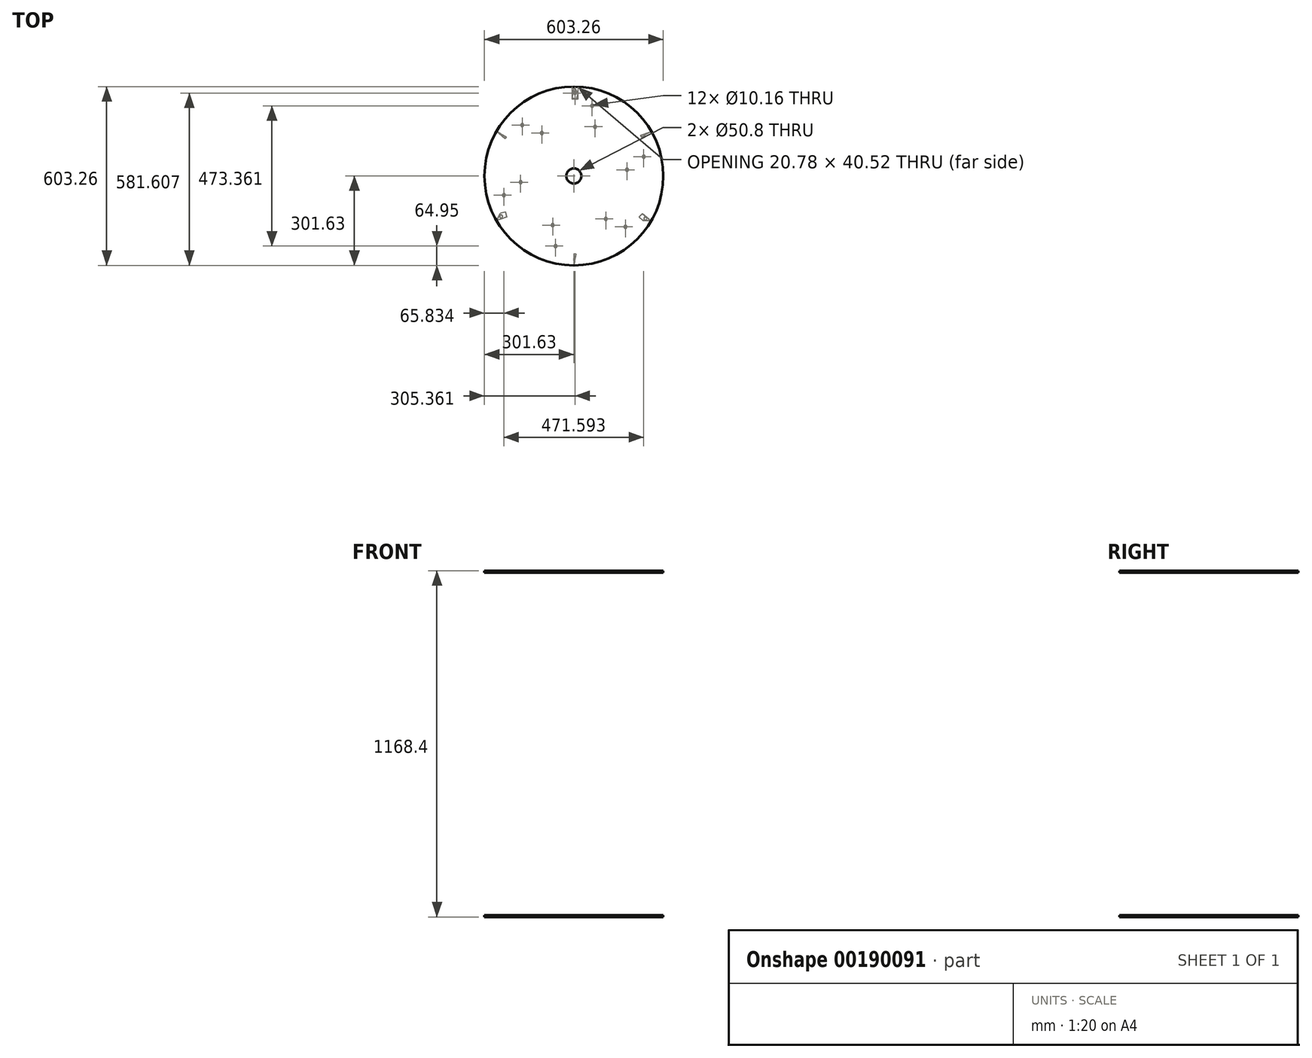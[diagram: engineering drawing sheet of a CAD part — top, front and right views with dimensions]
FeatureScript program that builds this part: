
annotation { "Feature Type Name" : "Feature", "Feature Type Description" : "" }
export const myFeature = defineFeature(function(context is Context, id is Id, definition is map)
    precondition{}
    {
        {
            var Q0;
            Q0=qCreatedBy(makeId("Top.planeOp"),FACE);
            var sketch = newSketch(context, id + "F0", { "sketchPlane" : qUnion([Q0])});
            skCircle(sketch, "E0", {"center": v(0, 0) * mm, "radius": 301.63 * mm});
            skCircle(sketch, "E1", {"center": v(0, 0) * mm, "radius": 25.4 * mm});
            skSolve(sketch);
        }
        {
            var Q0;
            Q0 = qSketchRegion(id + "F0", true);
            extrude(context, id + "F1", {"entities" : qUnion([Q0]), "depth" : 6.35 * mm});
        }
        {
            var Q0;
            Q0=makeQuery(id+"F1.opExtrude","CAP_FACE",FACE,{"disambiguationData":[OSD([sQuery(id+"F0.wireOp",EDGE,"E0"),sQuery(id+"F0.wireOp",EDGE,"E1")])],"isStart":false});
            var sketch = newSketch(context, id + "F2", { "sketchPlane" : qUnion([Q0])});
            skPoint(sketch, "E2.center", {"position": v(0, 0) * mm});
            skArc(sketch, "E3", {"start": v(87.34, 148.3) * mm, "mid": v(73.26, 252.31) * mm, "end": v(-19.74, 300.98) * mm});
            skArc(sketch, "E4", {"start": v(186.63, 0) * mm, "mid": v(255, 58.04) * mm, "end": v(260.45, 147.56) * mm});
            skArc(sketch, "E5", {"start": v(83.88, -151.75) * mm, "mid": v(170.95, -192) * mm, "end": v(258.02, -151.75) * mm});
            skArc(sketch, "E6", {"start": v(-87.35, -148.3) * mm, "mid": v(-78.67, -243.83) * mm, "end": v(-0.27, -299.1) * mm});
            skArc(sketch, "E7", {"start": v(-169.53, 0) * mm, "mid": v(-253.86, -64.43) * mm, "end": v(-248.85, -170.44) * mm});
            skArc(sketch, "E8", {"start": v(-88.68, 150.81) * mm, "mid": v(-172.82, 187.75) * mm, "end": v(-256.96, 150.81) * mm});
            skArc(sketch, "E9", {"start": v(-86.04, 153.57) * mm, "mid": v(-172.82, 191.56) * mm, "end": v(-259.6, 153.57) * mm});
            skLineSegment(sketch, "E10", {"start": v(-86.04, 153.57) * mm, "end": v(-88.68, 150.81) * mm});
            skLineSegment(sketch, "E11", {"start": v(-259.6, 153.57) * mm, "end": v(-256.96, 150.81) * mm});
            skLineSegment(sketch, "E12", {"start": v(0, 0) * mm, "end": v(-172.82, 73.45) * mm});
            skLineSegment(sketch, "E13", {"start": v(0, 0) * mm, "end": v(-20.32, 186.68) * mm});
            skLineSegment(sketch, "E14", {"start": v(0, 0) * mm, "end": v(152.79, 109.17) * mm});
            skLineSegment(sketch, "E15", {"start": v(0, 0) * mm, "end": v(170.95, -77.7) * mm});
            skLineSegment(sketch, "E16", {"start": v(0, 0) * mm, "end": v(20.32, -186.68) * mm});
            skLineSegment(sketch, "E17", {"start": v(0, 0) * mm, "end": v(-150.23, -112.66) * mm});
            skArc(sketch, "E18.1.0", {"start": v(-176.01, 2.28) * mm, "mid": v(-252.3, -53.88) * mm, "end": v(-262.8, -148.04) * mm});
            skArc(sketch, "E18.1.1", {"start": v(-174.95, -1.39) * mm, "mid": v(-249, -55.79) * mm, "end": v(-259.09, -147.13) * mm});
            skLineSegment(sketch, "E18.1.2", {"start": v(-176.01, 2.28) * mm, "end": v(-174.95, -1.39) * mm});
            skLineSegment(sketch, "E18.1.3", {"start": v(-262.8, -148.04) * mm, "end": v(-259.09, -147.13) * mm});
            skArc(sketch, "E18.2.0", {"start": v(-89.98, -151.3) * mm, "mid": v(-79.49, -245.45) * mm, "end": v(-3.2, -301.6) * mm});
            skArc(sketch, "E18.2.1", {"start": v(-86.27, -152.2) * mm, "mid": v(-76.2, -243.54) * mm, "end": v(-2.13, -297.94) * mm});
            skLineSegment(sketch, "E18.2.2", {"start": v(-89.98, -151.3) * mm, "end": v(-86.27, -152.2) * mm});
            skLineSegment(sketch, "E18.2.3", {"start": v(-3.2, -301.6) * mm, "end": v(-2.13, -297.94) * mm});
            skArc(sketch, "E18.3.0", {"start": v(86.04, -153.57) * mm, "mid": v(172.82, -191.56) * mm, "end": v(259.6, -153.57) * mm});
            skArc(sketch, "E18.3.1", {"start": v(88.68, -150.81) * mm, "mid": v(172.82, -187.75) * mm, "end": v(256.96, -150.81) * mm});
            skLineSegment(sketch, "E18.3.2", {"start": v(86.04, -153.57) * mm, "end": v(88.68, -150.81) * mm});
            skLineSegment(sketch, "E18.3.3", {"start": v(259.6, -153.57) * mm, "end": v(256.96, -150.81) * mm});
            skArc(sketch, "E18.4.0", {"start": v(176.01, -2.28) * mm, "mid": v(252.3, 53.88) * mm, "end": v(262.8, 148.04) * mm});
            skArc(sketch, "E18.4.1", {"start": v(174.95, 1.39) * mm, "mid": v(249, 55.79) * mm, "end": v(259.09, 147.13) * mm});
            skLineSegment(sketch, "E18.4.2", {"start": v(176.01, -2.28) * mm, "end": v(174.95, 1.39) * mm});
            skLineSegment(sketch, "E18.4.3", {"start": v(262.8, 148.04) * mm, "end": v(259.09, 147.13) * mm});
            skArc(sketch, "E18.5.0", {"start": v(89.98, 151.3) * mm, "mid": v(79.49, 245.45) * mm, "end": v(3.2, 301.6) * mm});
            skArc(sketch, "E18.5.1", {"start": v(86.27, 152.2) * mm, "mid": v(76.2, 243.54) * mm, "end": v(2.13, 297.94) * mm});
            skLineSegment(sketch, "E18.5.2", {"start": v(89.98, 151.3) * mm, "end": v(86.27, 152.2) * mm});
            skLineSegment(sketch, "E18.5.3", {"start": v(3.2, 301.6) * mm, "end": v(2.13, 297.94) * mm});
            skSolve(sketch);
        }
        {
            var Q0;
            Q0 = qSketchRegion(id + "F2", true);
            var Q1;
            Q1=sQuery(id+"F2.wireOp",EDGE,"E8");
            var Q2;
            Q2=sQuery(id+"F2.wireOp",EDGE,"E3");
            var Q3;
            Q3=sQuery(id+"F2.wireOp",EDGE,"E4");
            var Q4;
            Q4=sQuery(id+"F2.wireOp",EDGE,"E5");
            var Q5;
            Q5=sQuery(id+"F2.wireOp",EDGE,"E6");
            var Q6;
            Q6=sQuery(id+"F2.wireOp",EDGE,"E7");
            extrude(context, id + "F3", {"entities" : qUnion([Q0]), "bodyType" : ToolBodyType.SURFACE, "surfaceEntities" : qUnion([Q1, Q2, Q3, Q4, Q5, Q6]), "depth" : 1155.7 * mm});
        }
        {
            var Q0;
            Q0=makeQuery(id+"F1.opExtrude","CAP_FACE",FACE,{"disambiguationData":[OSD([sQuery(id+"F0.wireOp",EDGE,"E0"),sQuery(id+"F0.wireOp",EDGE,"E1")])],"isStart":false});
            cPlane(context, id + "F4", {"entities" : qUnion([Q0]), "cplaneType" : CPlaneType.OFFSET, "offset" : 1155.7 * mm, "width" : 152.4 * mm, "height" : 152.4 * mm});
        }
        {
            var Q0;
            Q0=qCreatedBy(id+"F4.planeOp",FACE);
            var sketch = newSketch(context, id + "F5", { "sketchPlane" : qUnion([Q0])});
            skCircle(sketch, "E19", {"center": v(0, 0) * mm, "radius": 301.63 * mm});
            skCircle(sketch, "E20", {"center": v(0, 0) * mm, "radius": 25.4 * mm});
            skSolve(sketch);
        }
        {
            var Q0;
            Q0=makeQuery(id+"F1.opExtrude","CAP_FACE",FACE,{"disambiguationData":[OSD([sQuery(id+"F0.wireOp",EDGE,"E0"),sQuery(id+"F0.wireOp",EDGE,"E1")])],"isStart":false});
            var sketch = newSketch(context, id + "F6", { "sketchPlane" : qUnion([Q0])});
            skLineSegment(sketch, "E21", {"start": v(261.58, 150.18) * mm, "end": v(167.94, 150.18) * mm});
            skLineSegment(sketch, "E22", {"start": v(0, 0) * mm, "end": v(0, -301.63) * mm});
            skLineSegment(sketch, "E23.1.0", {"start": v(0, 0) * mm, "end": v(261.21, 150.81) * mm});
            skLineSegment(sketch, "E23.2.0", {"start": v(0, 0) * mm, "end": v(-261.21, 150.81) * mm});
            skPoint(sketch, "E23.center", {"position": v(0, 0) * mm});
            skLineSegment(sketch, "E24", {"start": v(261.58, 150.18) * mm, "end": v(0, -301.63) * mm});
            skLineSegment(sketch, "E25", {"start": v(0, -301.63) * mm, "end": v(-261.21, 150.81) * mm});
            skLineSegment(sketch, "E26", {"start": v(-261.21, 150.81) * mm, "end": v(261.58, 150.18) * mm});
            skLineSegment(sketch, "E27.1.0", {"start": v(-261.26, -151.02) * mm, "end": v(0.32, 300.79) * mm});
            skLineSegment(sketch, "E27.1.1", {"start": v(0.32, 300.79) * mm, "end": v(261.53, -151.65) * mm});
            skLineSegment(sketch, "E27.1.2", {"start": v(261.53, -151.65) * mm, "end": v(-261.26, -151.02) * mm});
            skPoint(sketch, "E27.center", {"position": v(0.16, -0.42) * mm});
            skArc(sketch, "E28", {"start": v(-173.98, -0.28) * mm, "mid": v(-252.48, -55.47) * mm, "end": v(-261.26, -151.02) * mm});
            skLineSegment(sketch, "E29", {"start": v(-173.98, -0.28) * mm, "end": v(-153.56, -112.74) * mm});
            skLineSegment(sketch, "E30", {"start": v(-153.56, -112.74) * mm, "end": v(-261.26, -151.02) * mm});
            skLineSegment(sketch, "E31", {"start": v(-86.63, 150.6) * mm, "end": v(-174.01, 76.92) * mm});
            skLineSegment(sketch, "E32", {"start": v(-174.01, 76.92) * mm, "end": v(-261.21, 150.81) * mm});
            skLineSegment(sketch, "E33", {"start": v(0.32, 300.79) * mm, "end": v(-21, 188.5) * mm});
            skLineSegment(sketch, "E34", {"start": v(-21, 188.5) * mm, "end": v(86.9, 150.81) * mm});
            skLineSegment(sketch, "E35", {"start": v(174.63, 0) * mm, "end": v(153.71, 112.37) * mm});
            skLineSegment(sketch, "E36", {"start": v(153.71, 112.37) * mm, "end": v(261.58, 150.18) * mm});
            skLineSegment(sketch, "E37", {"start": v(86.95, -151.44) * mm, "end": v(174.33, -77.76) * mm});
            skLineSegment(sketch, "E38", {"start": v(174.33, -77.76) * mm, "end": v(261.53, -151.65) * mm});
            skLineSegment(sketch, "E39", {"start": v(0, -301.63) * mm, "end": v(21.86, -189.43) * mm});
            skLineSegment(sketch, "E40", {"start": v(21.86, -189.43) * mm, "end": v(-86.83, -151.23) * mm});
            skLineSegment(sketch, "E41", {"start": v(165.28, 37) * mm, "end": v(175.1, 0.19) * mm});
            skLineSegment(sketch, "E42", {"start": v(165.28, 37) * mm, "end": v(183.69, 41.9) * mm});
            skLineSegment(sketch, "E43", {"start": v(183.69, 41.9) * mm, "end": v(193.5, 5.1) * mm});
            skLineSegment(sketch, "E44", {"start": v(175.1, 0.19) * mm, "end": v(193.5, 5.1) * mm});
            skCircle(sketch, "E45", {"center": v(179.4, 21.05) * mm, "radius": 5.08 * mm});
            skLineSegment(sketch, "E46.1.0", {"start": v(87.39, 151.73) * mm, "end": v(92.34, 170.13) * mm});
            skLineSegment(sketch, "E46.1.1", {"start": v(50.6, 161.64) * mm, "end": v(87.39, 151.73) * mm});
            skLineSegment(sketch, "E46.1.2", {"start": v(55.55, 180.03) * mm, "end": v(92.34, 170.13) * mm});
            skCircle(sketch, "E46.1.3", {"center": v(71.47, 165.88) * mm, "radius": 5.08 * mm});
            skLineSegment(sketch, "E46.1.4", {"start": v(50.6, 161.64) * mm, "end": v(55.55, 180.03) * mm});
            skLineSegment(sketch, "E46.2.0", {"start": v(-87.71, 151.55) * mm, "end": v(-101.17, 165.03) * mm});
            skLineSegment(sketch, "E46.2.1", {"start": v(-114.68, 124.64) * mm, "end": v(-87.71, 151.55) * mm});
            skLineSegment(sketch, "E46.2.2", {"start": v(-128.14, 138.13) * mm, "end": v(-101.17, 165.03) * mm});
            skCircle(sketch, "E46.2.3", {"center": v(-107.93, 144.84) * mm, "radius": 5.08 * mm});
            skLineSegment(sketch, "E46.2.4", {"start": v(-114.68, 124.64) * mm, "end": v(-128.14, 138.13) * mm});
            skLineSegment(sketch, "E47.1.3.0", {"start": v(-175.1, -0.19) * mm, "end": v(-193.5, -5.1) * mm});
            skLineSegment(sketch, "E47.3.3.0", {"start": v(-165.28, -37) * mm, "end": v(-175.1, -0.19) * mm});
            skLineSegment(sketch, "E47.6.3.0", {"start": v(-183.69, -41.9) * mm, "end": v(-193.5, -5.1) * mm});
            skCircle(sketch, "E47.9.3.0", {"center": v(-179.4, -21.05) * mm, "radius": 5.08 * mm});
            skLineSegment(sketch, "E47.11.3.0", {"start": v(-165.28, -37) * mm, "end": v(-183.69, -41.9) * mm});
            skLineSegment(sketch, "E47.1.4.0", {"start": v(-87.39, -151.73) * mm, "end": v(-92.34, -170.13) * mm});
            skLineSegment(sketch, "E47.3.4.0", {"start": v(-50.6, -161.64) * mm, "end": v(-87.39, -151.73) * mm});
            skLineSegment(sketch, "E47.6.4.0", {"start": v(-55.55, -180.03) * mm, "end": v(-92.34, -170.13) * mm});
            skCircle(sketch, "E47.9.4.0", {"center": v(-71.47, -165.88) * mm, "radius": 5.08 * mm});
            skLineSegment(sketch, "E47.11.4.0", {"start": v(-50.6, -161.64) * mm, "end": v(-55.55, -180.03) * mm});
            skLineSegment(sketch, "E47.1.5.0", {"start": v(87.71, -151.55) * mm, "end": v(101.17, -165.03) * mm});
            skLineSegment(sketch, "E47.3.5.0", {"start": v(114.68, -124.64) * mm, "end": v(87.71, -151.55) * mm});
            skLineSegment(sketch, "E47.6.5.0", {"start": v(128.14, -138.13) * mm, "end": v(101.17, -165.03) * mm});
            skCircle(sketch, "E47.9.5.0", {"center": v(107.93, -144.84) * mm, "radius": 5.08 * mm});
            skLineSegment(sketch, "E47.11.5.0", {"start": v(114.68, -124.64) * mm, "end": v(128.14, -138.13) * mm});
            skLineSegment(sketch, "E48.MirrorCS", {"start": v(-9.55, -259.72) * mm, "end": v(-19.36, -296.53) * mm});
            skLineSegment(sketch, "E49.MirrorCS", {"start": v(-0.96, -301.44) * mm, "end": v(-19.36, -296.53) * mm});
            skCircle(sketch, "E50.MirrorC", {"center": v(-3.99, -280.82) * mm, "radius": 5.08 * mm});
            skLineSegment(sketch, "E51.MirrorCS", {"start": v(8.86, -264.62) * mm, "end": v(-9.55, -259.72) * mm});
            skLineSegment(sketch, "E52.MirrorCS", {"start": v(8.86, -264.62) * mm, "end": v(-0.96, -301.44) * mm});
            skLineSegment(sketch, "E53.1.0", {"start": v(260.57, -151.55) * mm, "end": v(247.12, -165.03) * mm});
            skLineSegment(sketch, "E53.1.1", {"start": v(220.15, -138.13) * mm, "end": v(247.12, -165.03) * mm});
            skLineSegment(sketch, "E53.1.2", {"start": v(233.6, -124.64) * mm, "end": v(260.57, -151.55) * mm});
            skLineSegment(sketch, "E53.1.3", {"start": v(233.6, -124.64) * mm, "end": v(220.15, -138.13) * mm});
            skCircle(sketch, "E53.1.4", {"center": v(241.2, -143.86) * mm, "radius": 5.08 * mm});
            skLineSegment(sketch, "E53.2.0", {"start": v(261.53, 149.9) * mm, "end": v(266.48, 131.5) * mm});
            skLineSegment(sketch, "E53.2.1", {"start": v(229.7, 121.6) * mm, "end": v(266.48, 131.5) * mm});
            skLineSegment(sketch, "E53.2.2", {"start": v(224.74, 139.99) * mm, "end": v(261.53, 149.9) * mm});
            skLineSegment(sketch, "E53.2.3", {"start": v(224.74, 139.99) * mm, "end": v(229.7, 121.6) * mm});
            skCircle(sketch, "E53.2.4", {"center": v(245.19, 136.96) * mm, "radius": 5.08 * mm});
            skLineSegment(sketch, "E54.2.3.0", {"start": v(0.96, 301.44) * mm, "end": v(19.36, 296.53) * mm});
            skLineSegment(sketch, "E54.3.3.0", {"start": v(9.55, 259.72) * mm, "end": v(19.36, 296.53) * mm});
            skLineSegment(sketch, "E54.6.3.0", {"start": v(-8.86, 264.62) * mm, "end": v(0.96, 301.44) * mm});
            skLineSegment(sketch, "E54.9.3.0", {"start": v(-8.86, 264.62) * mm, "end": v(9.55, 259.72) * mm});
            skCircle(sketch, "E54.12.3.0", {"center": v(3.99, 280.82) * mm, "radius": 5.08 * mm});
            skLineSegment(sketch, "E54.2.4.0", {"start": v(-260.57, 151.55) * mm, "end": v(-247.12, 165.03) * mm});
            skLineSegment(sketch, "E54.3.4.0", {"start": v(-220.15, 138.13) * mm, "end": v(-247.12, 165.03) * mm});
            skLineSegment(sketch, "E54.6.4.0", {"start": v(-233.6, 124.64) * mm, "end": v(-260.57, 151.55) * mm});
            skLineSegment(sketch, "E54.9.4.0", {"start": v(-233.6, 124.64) * mm, "end": v(-220.15, 138.13) * mm});
            skCircle(sketch, "E54.12.4.0", {"center": v(-241.2, 143.86) * mm, "radius": 5.08 * mm});
            skLineSegment(sketch, "E54.2.5.0", {"start": v(-261.53, -149.9) * mm, "end": v(-266.48, -131.5) * mm});
            skLineSegment(sketch, "E54.3.5.0", {"start": v(-229.7, -121.6) * mm, "end": v(-266.48, -131.5) * mm});
            skLineSegment(sketch, "E54.6.5.0", {"start": v(-224.74, -139.99) * mm, "end": v(-261.53, -149.9) * mm});
            skLineSegment(sketch, "E54.9.5.0", {"start": v(-224.74, -139.99) * mm, "end": v(-229.7, -121.6) * mm});
            skCircle(sketch, "E54.12.5.0", {"center": v(-245.19, -136.96) * mm, "radius": 5.08 * mm});
            skCircle(sketch, "E55", {"center": v(-61.65, -236.68) * mm, "radius": 5.08 * mm});
            skLineSegment(sketch, "E56", {"start": v(-78.31, -246.3) * mm, "end": v(-83.08, -238.05) * mm});
            skLineSegment(sketch, "E57", {"start": v(-83.08, -238.05) * mm, "end": v(-50.08, -219) * mm});
            skLineSegment(sketch, "E58", {"start": v(-50.08, -219) * mm, "end": v(-40.56, -235.5) * mm});
            skLineSegment(sketch, "E59", {"start": v(-40.56, -235.5) * mm, "end": v(-73.55, -254.55) * mm});
            skLineSegment(sketch, "E60", {"start": v(-73.55, -254.55) * mm, "end": v(-83.08, -238.05) * mm});
            skLineSegment(sketch, "E61.1.0", {"start": v(164.62, -152.87) * mm, "end": v(183.67, -152.87) * mm});
            skLineSegment(sketch, "E61.1.1", {"start": v(164.62, -190.97) * mm, "end": v(164.62, -152.87) * mm});
            skCircle(sketch, "E61.1.2", {"center": v(174.15, -171.73) * mm, "radius": 5.08 * mm});
            skLineSegment(sketch, "E61.1.3", {"start": v(183.67, -152.87) * mm, "end": v(183.67, -190.97) * mm});
            skLineSegment(sketch, "E61.1.4", {"start": v(174.15, -190.97) * mm, "end": v(164.62, -190.97) * mm});
            skLineSegment(sketch, "E61.1.5", {"start": v(183.67, -190.97) * mm, "end": v(164.62, -190.97) * mm});
            skLineSegment(sketch, "E61.2.0", {"start": v(214.7, 66.13) * mm, "end": v(224.23, 82.63) * mm});
            skLineSegment(sketch, "E61.2.1", {"start": v(247.7, 47.08) * mm, "end": v(214.7, 66.13) * mm});
            skCircle(sketch, "E61.2.2", {"center": v(235.8, 64.95) * mm, "radius": 5.08 * mm});
            skLineSegment(sketch, "E61.2.3", {"start": v(224.23, 82.63) * mm, "end": v(257.22, 63.58) * mm});
            skLineSegment(sketch, "E61.2.4", {"start": v(252.46, 55.33) * mm, "end": v(247.7, 47.08) * mm});
            skLineSegment(sketch, "E61.2.5", {"start": v(257.22, 63.58) * mm, "end": v(247.7, 47.08) * mm});
            skLineSegment(sketch, "E61.3.0", {"start": v(50.08, 219) * mm, "end": v(40.56, 235.5) * mm});
            skLineSegment(sketch, "E61.3.1", {"start": v(83.08, 238.05) * mm, "end": v(50.08, 219) * mm});
            skCircle(sketch, "E61.3.2", {"center": v(61.65, 236.68) * mm, "radius": 5.08 * mm});
            skLineSegment(sketch, "E61.3.3", {"start": v(40.56, 235.5) * mm, "end": v(73.55, 254.55) * mm});
            skLineSegment(sketch, "E61.3.4", {"start": v(78.31, 246.3) * mm, "end": v(83.08, 238.05) * mm});
            skLineSegment(sketch, "E61.3.5", {"start": v(73.55, 254.55) * mm, "end": v(83.08, 238.05) * mm});
            skLineSegment(sketch, "E61.4.0", {"start": v(-164.62, 152.87) * mm, "end": v(-183.67, 152.87) * mm});
            skLineSegment(sketch, "E61.4.1", {"start": v(-164.62, 190.97) * mm, "end": v(-164.62, 152.87) * mm});
            skCircle(sketch, "E61.4.2", {"center": v(-174.15, 171.73) * mm, "radius": 5.08 * mm});
            skLineSegment(sketch, "E61.4.3", {"start": v(-183.67, 152.87) * mm, "end": v(-183.67, 190.97) * mm});
            skLineSegment(sketch, "E61.4.4", {"start": v(-174.15, 190.97) * mm, "end": v(-164.62, 190.97) * mm});
            skLineSegment(sketch, "E61.4.5", {"start": v(-183.67, 190.97) * mm, "end": v(-164.62, 190.97) * mm});
            skLineSegment(sketch, "E61.5.0", {"start": v(-214.7, -66.13) * mm, "end": v(-224.23, -82.63) * mm});
            skLineSegment(sketch, "E61.5.1", {"start": v(-247.7, -47.08) * mm, "end": v(-214.7, -66.13) * mm});
            skCircle(sketch, "E61.5.2", {"center": v(-235.8, -64.95) * mm, "radius": 5.08 * mm});
            skLineSegment(sketch, "E61.5.3", {"start": v(-224.23, -82.63) * mm, "end": v(-257.22, -63.58) * mm});
            skLineSegment(sketch, "E61.5.4", {"start": v(-252.46, -55.33) * mm, "end": v(-247.7, -47.08) * mm});
            skLineSegment(sketch, "E61.5.5", {"start": v(-257.22, -63.58) * mm, "end": v(-247.7, -47.08) * mm});
            skSolve(sketch);
        }
        {
            var Q0;
            Q0 = qSketchRegion(id + "F5", true);
            extrude(context, id + "F7", {"entities" : qUnion([Q0]), "depth" : 6.35 * mm});
        }
        {
            var Q0;
            Q0=makeQuery(id+"F6.imprint","IMPRINT",FACE,{"disambiguationData":[TD([[makeQuery(id+"F6.imprint","IMPRINT",EDGE,{"derivedFrom":sQuery(id+"F6.wireOp",EDGE,"E54.12.4.0")}),-1.0]])]});
            var Q1;
            Q1=makeQuery(id+"F6.imprint","IMPRINT",FACE,{"disambiguationData":[TD([[makeQuery(id+"F6.imprint","IMPRINT",EDGE,{"derivedFrom":sQuery(id+"F6.wireOp",EDGE,"E61.4.2")}),1.0]])]});
            var Q2;
            Q2=makeQuery(id+"F6.imprint","IMPRINT",FACE,{"disambiguationData":[TD([[makeQuery(id+"F6.imprint","IMPRINT",EDGE,{"derivedFrom":sQuery(id+"F6.wireOp",EDGE,"E46.2.3")}),1.0]])]});
            var Q3;
            Q3=makeQuery(id+"F6.imprint","IMPRINT",FACE,{"disambiguationData":[TD([[makeQuery(id+"F6.imprint","IMPRINT",EDGE,{"derivedFrom":sQuery(id+"F6.wireOp",EDGE,"E54.12.5.0")}),-1.0]])]});
            var Q4;
            Q4=makeQuery(id+"F6.imprint","IMPRINT",FACE,{"disambiguationData":[TD([[makeQuery(id+"F6.imprint","IMPRINT",EDGE,{"derivedFrom":sQuery(id+"F6.wireOp",EDGE,"E61.5.2")}),1.0]])]});
            var Q5;
            Q5=makeQuery(id+"F6.imprint","IMPRINT",FACE,{"disambiguationData":[TD([[makeQuery(id+"F6.imprint","IMPRINT",EDGE,{"derivedFrom":sQuery(id+"F6.wireOp",EDGE,"E47.9.3.0")}),1.0]])]});
            var Q6;
            Q6=makeQuery(id+"F6.imprint","IMPRINT",FACE,{"disambiguationData":[TD([[makeQuery(id+"F6.imprint","IMPRINT",EDGE,{"derivedFrom":sQuery(id+"F6.wireOp",EDGE,"E50.MirrorC")}),-1.0]])]});
            var Q7;
            Q7=makeQuery(id+"F6.imprint","IMPRINT",FACE,{"disambiguationData":[TD([[makeQuery(id+"F6.imprint","IMPRINT",EDGE,{"derivedFrom":sQuery(id+"F6.wireOp",EDGE,"E55")}),1.0]])]});
            var Q8;
            Q8=makeQuery(id+"F6.imprint","IMPRINT",FACE,{"disambiguationData":[TD([[makeQuery(id+"F6.imprint","IMPRINT",EDGE,{"derivedFrom":sQuery(id+"F6.wireOp",EDGE,"E47.9.4.0")}),1.0]])]});
            var Q9;
            Q9=makeQuery(id+"F6.imprint","IMPRINT",FACE,{"disambiguationData":[TD([[makeQuery(id+"F6.imprint","IMPRINT",EDGE,{"derivedFrom":sQuery(id+"F6.wireOp",EDGE,"E47.9.5.0")}),1.0]])]});
            var Q10;
            Q10=makeQuery(id+"F6.imprint","IMPRINT",FACE,{"disambiguationData":[TD([[makeQuery(id+"F6.imprint","IMPRINT",EDGE,{"derivedFrom":sQuery(id+"F6.wireOp",EDGE,"E61.1.2")}),1.0]])]});
            var Q11;
            Q11=makeQuery(id+"F6.imprint","IMPRINT",FACE,{"disambiguationData":[TD([[makeQuery(id+"F6.imprint","IMPRINT",EDGE,{"derivedFrom":sQuery(id+"F6.wireOp",EDGE,"E53.1.4")}),-1.0]])]});
            var Q12;
            Q12=makeQuery(id+"F6.imprint","IMPRINT",FACE,{"disambiguationData":[TD([[makeQuery(id+"F6.imprint","IMPRINT",EDGE,{"derivedFrom":sQuery(id+"F6.wireOp",EDGE,"E45")}),1.0]])]});
            var Q13;
            Q13=makeQuery(id+"F6.imprint","IMPRINT",FACE,{"disambiguationData":[TD([[makeQuery(id+"F6.imprint","IMPRINT",EDGE,{"derivedFrom":sQuery(id+"F6.wireOp",EDGE,"E61.2.2")}),1.0]])]});
            var Q14;
            Q14=makeQuery(id+"F6.imprint","IMPRINT",FACE,{"disambiguationData":[TD([[makeQuery(id+"F6.imprint","IMPRINT",EDGE,{"derivedFrom":sQuery(id+"F6.wireOp",EDGE,"E53.2.4")}),-1.0]])]});
            var Q15;
            Q15=makeQuery(id+"F6.imprint","IMPRINT",FACE,{"disambiguationData":[TD([[makeQuery(id+"F6.imprint","IMPRINT",EDGE,{"derivedFrom":sQuery(id+"F6.wireOp",EDGE,"E46.1.3")}),1.0]])]});
            var Q16;
            Q16=makeQuery(id+"F6.imprint","IMPRINT",FACE,{"disambiguationData":[TD([[makeQuery(id+"F6.imprint","IMPRINT",EDGE,{"derivedFrom":sQuery(id+"F6.wireOp",EDGE,"E61.3.2")}),1.0]])]});
            var Q17;
            Q17=makeQuery(id+"F6.imprint","IMPRINT",FACE,{"disambiguationData":[TD([[makeQuery(id+"F6.imprint","IMPRINT",EDGE,{"derivedFrom":sQuery(id+"F6.wireOp",EDGE,"E54.12.3.0")}),-1.0]])]});
            var Q18;
            Q18=sQuery(id+"F6.wireOp",EDGE,"E54.12.5.0");
            var Q19;
            Q19=sQuery(id+"F6.wireOp",EDGE,"E61.5.2");
            var Q20;
            Q20=sQuery(id+"F6.wireOp",EDGE,"E47.9.3.0");
            var Q21;
            Q21=sQuery(id+"F6.wireOp",EDGE,"E54.12.4.0");
            var Q22;
            Q22=sQuery(id+"F6.wireOp",EDGE,"E61.4.2");
            var Q23;
            Q23=sQuery(id+"F6.wireOp",EDGE,"E46.2.3");
            var Q24;
            Q24=sQuery(id+"F6.wireOp",EDGE,"E54.12.3.0");
            var Q25;
            Q25=sQuery(id+"F6.wireOp",EDGE,"E61.3.2");
            var Q26;
            Q26=sQuery(id+"F6.wireOp",EDGE,"E46.1.3");
            var Q27;
            Q27=sQuery(id+"F6.wireOp",EDGE,"E53.2.4");
            var Q28;
            Q28=sQuery(id+"F6.wireOp",EDGE,"E61.2.2");
            var Q29;
            Q29=sQuery(id+"F6.wireOp",EDGE,"E45");
            var Q30;
            Q30=sQuery(id+"F6.wireOp",EDGE,"E53.1.4");
            var Q31;
            Q31=sQuery(id+"F6.wireOp",EDGE,"E61.1.2");
            var Q32;
            Q32=sQuery(id+"F6.wireOp",EDGE,"E47.9.5.0");
            var Q33;
            Q33=sQuery(id+"F6.wireOp",EDGE,"E50.MirrorC");
            var Q34;
            Q34=sQuery(id+"F6.wireOp",EDGE,"E55");
            var Q35;
            Q35=sQuery(id+"F6.wireOp",EDGE,"E47.9.4.0");
            extrude(context, id + "F8", {"entities" : qUnion([Q0, Q1, Q2, Q3, Q4, Q5, Q6, Q7, Q8, Q9, Q10, Q11, Q12, Q13, Q14, Q15, Q16, Q17]), "operationType" : NewBodyOperationType.REMOVE, "surfaceEntities" : qUnion([Q18, Q19, Q20, Q21, Q22, Q23, Q24, Q25, Q26, Q27, Q28, Q29, Q30, Q31, Q32, Q33, Q34, Q35]), "endBound" : BoundingType.THROUGH_ALL, "oppositeDirection" : true, "depth" : 25.4 * mm});
        }
    });
